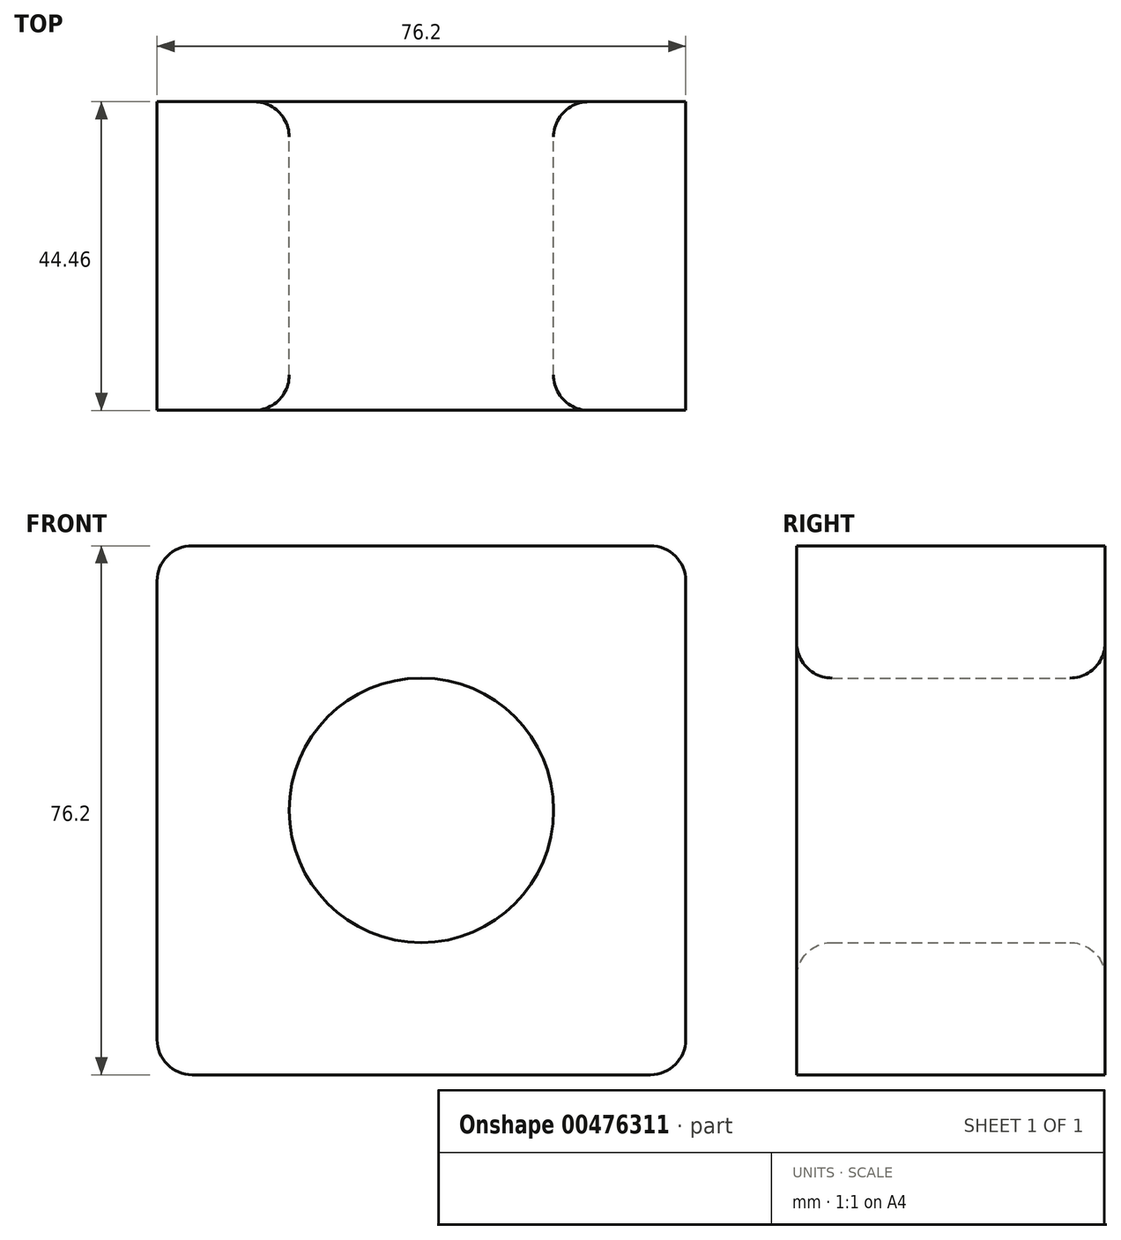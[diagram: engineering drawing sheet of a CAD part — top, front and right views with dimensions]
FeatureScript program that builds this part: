
annotation { "Feature Type Name" : "Feature", "Feature Type Description" : "" }
export const myFeature = defineFeature(function(context is Context, id is Id, definition is map)
    precondition{}
    {
        {
            var Q0;
            Q0=qCreatedBy(makeId("Front.planeOp"),FACE);
            var sketch = newSketch(context, id + "F0", { "sketchPlane" : qUnion([Q0])});
            skLineSegment(sketch, "E0.bottom", {"start": v(38.1, 38.1) * mm, "end": v(-38.1, 38.1) * mm});
            skLineSegment(sketch, "E0.top", {"start": v(38.1, -38.1) * mm, "end": v(-38.1, -38.1) * mm});
            skLineSegment(sketch, "E0.left", {"start": v(38.1, 38.1) * mm, "end": v(38.1, -38.1) * mm});
            skLineSegment(sketch, "E0.right", {"start": v(-38.1, 38.1) * mm, "end": v(-38.1, -38.1) * mm});
            skPoint(sketch, "E0.middle", {"position": v(0, 0) * mm});
            skCircle(sketch, "E1", {"center": v(0, 0) * mm, "radius": 19.05 * mm});
            skSolve(sketch);
        }
        {
            var Q0;
            Q0=makeQuery(id+"F0.imprint","IMPRINT",FACE,{"disambiguationData":[TD([[makeQuery(id+"F0.imprint","IMPRINT",EDGE,{"derivedFrom":sQuery(id+"F0.wireOp",EDGE,"E0.bottom")}),1.0]])]});
            extrude(context, id + "F1", {"entities" : qUnion([Q0]), "endBound" : BoundingType.SYMMETRIC, "depth" : 44.45 * mm});
        }
        {
            var Q0;
            Q0=makeQuery(id+"F1.opExtrude","SWEPT_EDGE",EDGE,{"disambiguationData":[OSD([sQuery(id+"F0.wireOp",EDGE,"E0.bottom"),sQuery(id+"F0.wireOp",EDGE,"E0.left")])]});
            var Q1;
            Q1=makeQuery(id+"F1.opExtrude","SWEPT_EDGE",EDGE,{"disambiguationData":[OSD([sQuery(id+"F0.wireOp",EDGE,"E0.bottom"),sQuery(id+"F0.wireOp",EDGE,"E0.right")])]});
            var Q2;
            Q2=makeQuery(id+"F1.opExtrude","SWEPT_EDGE",EDGE,{"disambiguationData":[OSD([sQuery(id+"F0.wireOp",EDGE,"E0.top"),sQuery(id+"F0.wireOp",EDGE,"E0.left")])]});
            var Q3;
            Q3=makeQuery(id+"F1.opExtrude","SWEPT_EDGE",EDGE,{"disambiguationData":[OSD([sQuery(id+"F0.wireOp",EDGE,"E0.top"),sQuery(id+"F0.wireOp",EDGE,"E0.right")])]});
            var Q4;
            Q4=makeQuery(id+"F1.opExtrude","CAP_EDGE",EDGE,{"disambiguationData":[OSD([sQuery(id+"F0.wireOp",EDGE,"E1")])],"isStart":false});
            var Q5;
            Q5=makeQuery(id+"F1.opExtrude","CAP_EDGE",EDGE,{"disambiguationData":[OSD([sQuery(id+"F0.wireOp",EDGE,"E1")])],"isStart":true});
            fillet(context, id + "F2", {"entities" : qUnion([Q0, Q1, Q2, Q3, Q4, Q5]), "radius" : 5.08 * mm, "tangentPropagation" : true, "allowEdgeOverflow" : false});
        }
    });
